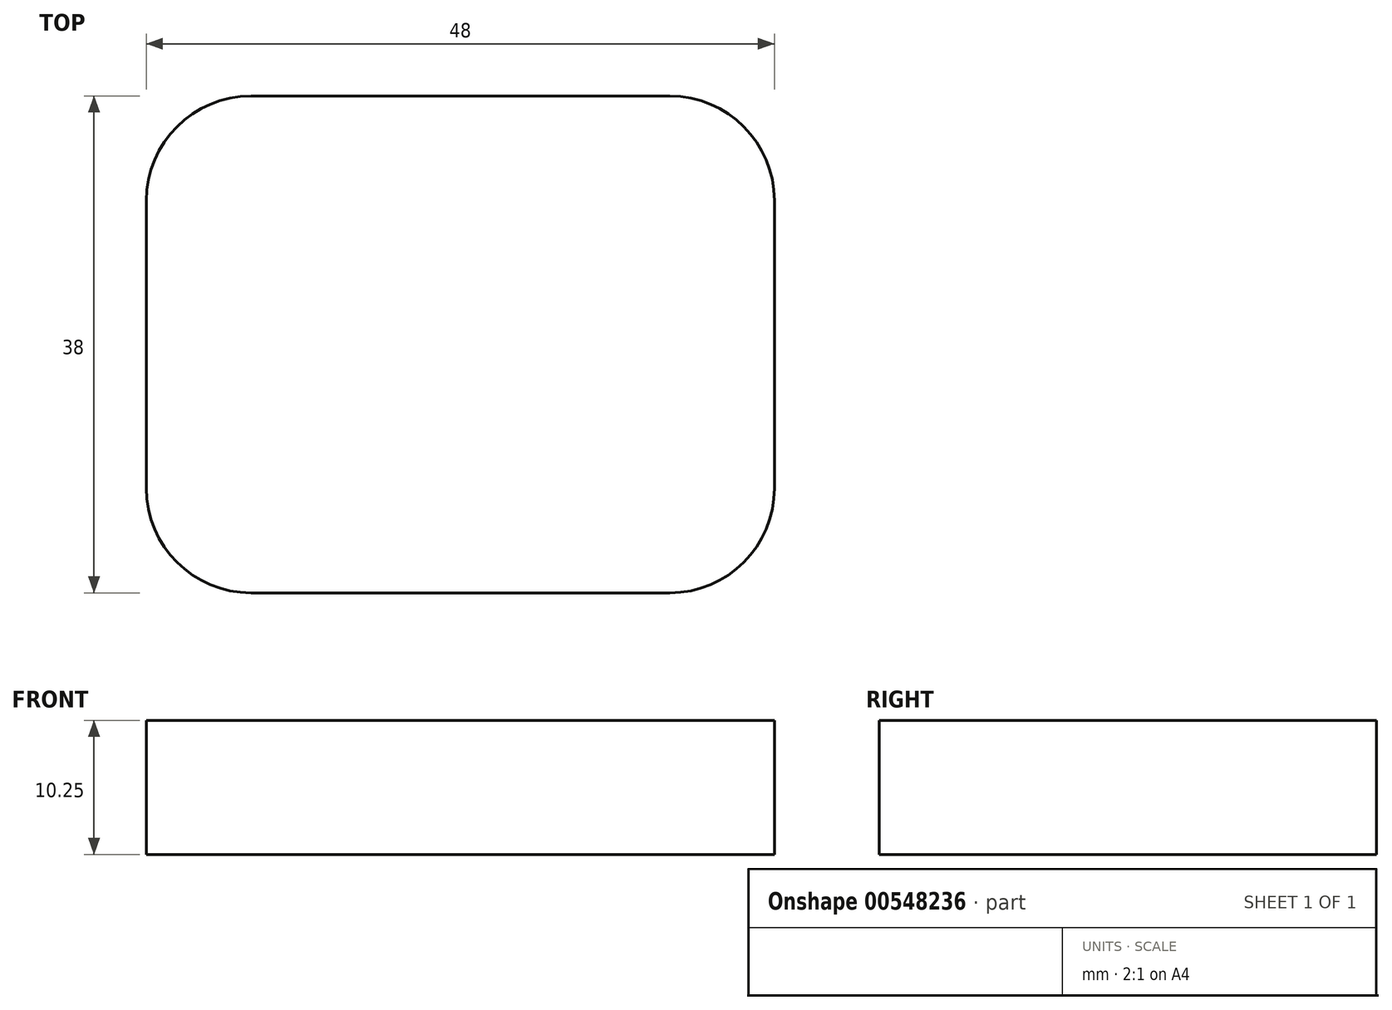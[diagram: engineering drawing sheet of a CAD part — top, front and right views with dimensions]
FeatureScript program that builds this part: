
annotation { "Feature Type Name" : "Feature", "Feature Type Description" : "" }
export const myFeature = defineFeature(function(context is Context, id is Id, definition is map)
    precondition{}
    {
        {
            var Q0;
            Q0=qCreatedBy(makeId("Top.planeOp"),FACE);
            var sketch = newSketch(context, id + "F0", { "sketchPlane" : qUnion([Q0])});
            skLineSegment(sketch, "E0.bottom", {"start": v(-16, 19) * mm, "end": v(16, 19) * mm});
            skLineSegment(sketch, "E0.top", {"start": v(-16, -19) * mm, "end": v(16, -19) * mm});
            skLineSegment(sketch, "E0.left", {"start": v(-24, 11) * mm, "end": v(-24, -11) * mm});
            skLineSegment(sketch, "E0.right", {"start": v(24, 11) * mm, "end": v(24, -11) * mm});
            skPoint(sketch, "E1.visualSharp", {"position": v(24, 19) * mm});
            skArc(sketch, "E1.filletArc", {"start": v(24, 11) * mm, "mid": v(21.66, 16.66) * mm, "end": v(16, 19) * mm});
            skPoint(sketch, "E2.visualSharp", {"position": v(24, -19) * mm});
            skArc(sketch, "E2.filletArc", {"start": v(16, -19) * mm, "mid": v(21.66, -16.66) * mm, "end": v(24, -11) * mm});
            skPoint(sketch, "E3.visualSharp", {"position": v(-24, -19) * mm});
            skArc(sketch, "E3.filletArc", {"start": v(-24, -11) * mm, "mid": v(-21.66, -16.66) * mm, "end": v(-16, -19) * mm});
            skPoint(sketch, "E4.visualSharp", {"position": v(-24, 19) * mm});
            skArc(sketch, "E4.filletArc", {"start": v(-16, 19) * mm, "mid": v(-21.66, 16.66) * mm, "end": v(-24, 11) * mm});
            skSolve(sketch);
        }
        {
            var Q0;
            Q0 = qSketchRegion(id + "F0", true);
            extrude(context, id + "F1", {"entities" : qUnion([Q0]), "depth" : 10.25 * mm, "offsetDistance" : 25 * mm});
        }
    });
